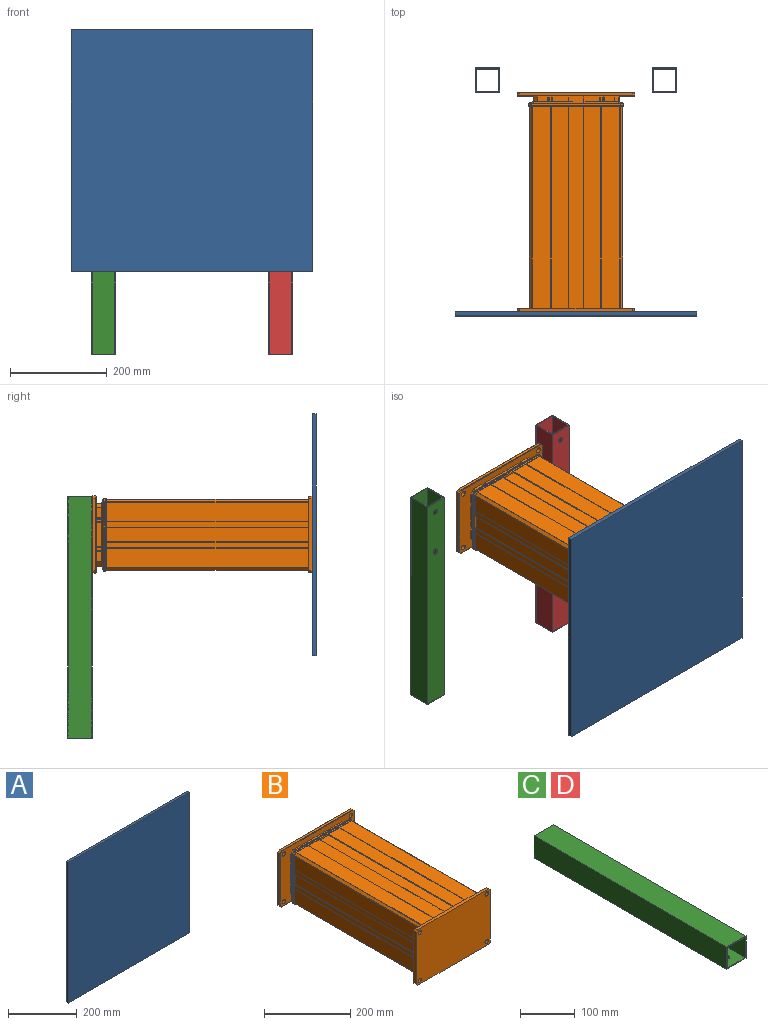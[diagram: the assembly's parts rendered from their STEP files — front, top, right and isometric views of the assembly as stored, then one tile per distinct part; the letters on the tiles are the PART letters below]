
ASSEMBLY  parts=4 mates=3
PART A: 6 faces, bbox 500x8x500 mm
  f0: plane 500x8mm, normal (0,0,1), area 4000mm2, adj f1,f3,f4,f5
  f1: plane 500x8mm, normal (-1,0,0), area 4000mm2, adj f0,f2,f4,f5
  f2: plane 500x8mm, normal (0,0,-1), area 4000mm2, adj f1,f3,f4,f5
  f3: plane 500x8mm, normal (1,0,0), area 4000mm2, adj f0,f2,f4,f5
  f4: plane 500x500mm, normal (0,-1,0), area 250000mm2, adj f0,f1,f2,f3
  f5: plane 500x500mm, normal (0,1,0), area 250000mm2, adj f0,f1,f2,f3
PART B: 367 faces, bbox 245x456x161 mm
  f0: plane 8x4.41mm, normal (0.71,0,0.71), area 49.9mm2, adj f357,f360,f361,f366
  f1: plane 8x4.41mm, normal (0.71,0,-0.71), area 49.9mm2, adj f357,f358,f361,f366
  f2: plane 8x4.41mm, normal (-0.71,0,-0.71), area 49.9mm2, adj f358,f359,f361,f366
  f3: plane 8x4.41mm, normal (-0.71,0,0.71), area 49.9mm2, adj f359,f360,f361,f366
  f4: plane 417x30.8mm, normal (1,0,0), area 12843.6mm2, adj f10,f11,f75,f361
  f5: cylinder r=0.5mm len=417mm, axis (0,1,0), area 491.3mm2, adj f74,f75,f342,f361
  f6: cylinder r=0.5mm len=417mm, axis (0,1,0), area 491.3mm2, adj f22,f23,f75,f361
  f7: cylinder r=0.5mm len=417mm, axis (0,-1,0), area 491.3mm2, adj f23,f24,f75,f361
  f8: cylinder r=0.5mm len=417mm, axis (0,1,0), area 163.8mm2, adj f26,f27,f75,f361
  f9: cylinder r=0.5mm len=417mm, axis (0,1,0), area 163.8mm2, adj f35,f36,f75,f361
  f10: cylinder r=0.5mm len=417mm, axis (0,-1,0), area 491.3mm2, adj f4,f38,f75,f361
  f11: cylinder r=0.5mm len=417mm, axis (0,1,0), area 491.3mm2, adj f4,f39,f75,f361
  f12: cylinder r=0.5mm len=417mm, axis (0,1,0), area 491.3mm2, adj f55,f56,f75,f361
  f13: cylinder r=0.5mm len=417mm, axis (0,-1,0), area 491.3mm2, adj f56,f57,f75,f361
  f14: cylinder r=0.5mm len=417mm, axis (0,-1,0), area 491.3mm2, adj f73,f74,f75,f361
  f15: plane 15.7x0.21mm, normal (0.71,0,-0.71), area 4.6mm2, adj f16,f18,f84,f313
  f16: cylinder r=0.5mm len=15.7mm, axis (0,-1,0), area 6.2mm2, adj f15,f17,f84,f313
  f17: plane 29.59x15.7mm, normal (0,0,-1), area 430.9mm2, adj f16,f81,f84,f167,f312,f313,f319
  f18: cylinder r=0.5mm len=15.7mm, axis (0,1,0), area 6.2mm2, adj f15,f84,f313,f356
  f19: plane 132.51x82.11mm, normal (0,1,0), area 403.8mm2, adj f80,f168,f169,f170,f171,f172,f173,f174
  f20: plane 417x35.73mm, normal (0,0,-1), area 14898.9mm2, adj f21,f75,f355,f361
  f21: cylinder r=0.5mm len=417mm, axis (0,-1,0), area 491.3mm2, adj f20,f22,f75,f361
  f22: plane 417x1.04mm, normal (0.71,0,0.71), area 615mm2, adj f6,f21,f75,f361
  f23: plane 417x30.8mm, normal (0,0,-1), area 12843.6mm2, adj f6,f7,f75,f361
  f24: plane 417x1.04mm, normal (-0.71,0,0.71), area 615mm2, adj f7,f25,f75,f361
  f25: cylinder r=0.5mm len=417mm, axis (0,1,0), area 491.3mm2, adj f24,f26,f75,f361
  f26: plane 417x35.73mm, normal (0,0,-1), area 14898.9mm2, adj f8,f25,f75,f361
  f27: plane 417x0.21mm, normal (-0.71,0,-0.71), area 122.1mm2, adj f8,f28,f75,f361
  f28: cylinder r=0.5mm len=417mm, axis (0,-1,0), area 163.8mm2, adj f27,f29,f75,f361
  f29: plane 417x38.88mm, normal (0,0,-1), area 16212.4mm2, adj f28,f30,f75,f361
  f30: cylinder r=1mm len=417mm, axis (0,-1,0), area 327.5mm2, adj f29,f31,f75,f361
  f31: plane 417x5.41mm, normal (0.71,0,-0.71), area 3192.9mm2, adj f30,f32,f75,f361
  f32: cylinder r=1mm len=417mm, axis (0,-1,0), area 327.5mm2, adj f31,f33,f75,f361
  f33: plane 417x38.88mm, normal (1,0,0), area 16212.4mm2, adj f32,f34,f75,f361
  f34: cylinder r=0.5mm len=417mm, axis (0,-1,0), area 163.8mm2, adj f33,f35,f75,f361
  f35: plane 417x0.21mm, normal (0.71,0,0.71), area 122.1mm2, adj f9,f34,f75,f361
  f36: plane 417x12.23mm, normal (1,0,0), area 5099.4mm2, adj f9,f37,f75,f361
  f37: cylinder r=0.5mm len=417mm, axis (0,-1,0), area 491.3mm2, adj f36,f38,f75,f361
  f38: plane 417x1.04mm, normal (-0.71,0,0.71), area 615mm2, adj f10,f37,f75,f361
  f39: plane 417x1.04mm, normal (-0.71,0,-0.71), area 615mm2, adj f11,f40,f75,f361
  f40: cylinder r=0.5mm len=417mm, axis (0,1,0), area 491.3mm2, adj f39,f41,f75,f361
  f41: plane 417x12.23mm, normal (1,0,0), area 5099.4mm2, adj f40,f42,f75,f361
  f42: cylinder r=0.5mm len=417mm, axis (0,-1,0), area 163.8mm2, adj f41,f43,f75,f361
  f43: plane 417x0.21mm, normal (0.71,0,-0.71), area 122.1mm2, adj f42,f44,f75,f361
  f44: cylinder r=0.5mm len=417mm, axis (0,1,0), area 163.8mm2, adj f43,f45,f75,f361
  f45: plane 417x38.88mm, normal (1,0,0), area 16212.4mm2, adj f44,f46,f75,f361
  f46: cylinder r=1mm len=417mm, axis (0,1,0), area 327.5mm2, adj f45,f47,f75,f361
  f47: plane 417x5.41mm, normal (0.71,0,0.71), area 3192.9mm2, adj f46,f48,f75,f361
  f48: cylinder r=1mm len=417mm, axis (0,1,0), area 327.5mm2, adj f47,f49,f75,f361
  f49: plane 417x38.88mm, normal (0,0,1), area 16212.4mm2, adj f48,f50,f75,f361
  f50: cylinder r=0.5mm len=417mm, axis (0,1,0), area 163.8mm2, adj f49,f51,f75,f361
  f51: plane 417x0.21mm, normal (-0.71,0,0.71), area 122.1mm2, adj f50,f52,f75,f361
  f52: cylinder r=0.5mm len=417mm, axis (0,-1,0), area 163.8mm2, adj f51,f53,f75,f361
  f53: plane 417x35.73mm, normal (0,0,1), area 14898.9mm2, adj f52,f54,f75,f361
  f54: cylinder r=0.5mm len=417mm, axis (0,-1,0), area 491.3mm2, adj f53,f55,f75,f361
  f55: plane 417x1.04mm, normal (-0.71,0,-0.71), area 615mm2, adj f12,f54,f75,f361
  f56: plane 417x30.8mm, normal (0,0,1), area 12843.6mm2, adj f12,f13,f75,f361
  f57: plane 417x1.04mm, normal (0.71,0,-0.71), area 615mm2, adj f13,f58,f75,f361
  f58: cylinder r=0.5mm len=417mm, axis (0,1,0), area 491.3mm2, adj f57,f59,f75,f361
  f59: plane 417x35.73mm, normal (0,0,1), area 14898.9mm2, adj f58,f60,f75,f361
  f60: cylinder r=0.5mm len=417mm, axis (0,1,0), area 163.8mm2, adj f59,f61,f75,f361
  f61: plane 417x0.21mm, normal (0.71,0,0.71), area 122.1mm2, adj f60,f62,f75,f361
  f62: cylinder r=0.5mm len=417mm, axis (0,-1,0), area 163.8mm2, adj f61,f63,f75,f361
  f63: plane 417x38.88mm, normal (0,0,1), area 16212.4mm2, adj f62,f64,f75,f361
  f64: cylinder r=1mm len=417mm, axis (0,-1,0), area 327.5mm2, adj f63,f65,f75,f361
  f65: plane 417x5.41mm, normal (-0.71,0,0.71), area 3192.9mm2, adj f64,f66,f75,f361
  f66: cylinder r=1mm len=417mm, axis (0,-1,0), area 327.5mm2, adj f65,f67,f75,f361
  f67: plane 417x38.88mm, normal (-1,0,0), area 16212.4mm2, adj f66,f68,f75,f361
  f68: cylinder r=0.5mm len=417mm, axis (0,-1,0), area 163.8mm2, adj f67,f69,f75,f361
  f69: plane 417x0.21mm, normal (-0.71,0,-0.71), area 122.1mm2, adj f68,f70,f75,f361
  f70: cylinder r=0.5mm len=417mm, axis (0,1,0), area 163.8mm2, adj f69,f71,f75,f361
  f71: plane 417x12.23mm, normal (-1,0,0), area 5099.4mm2, adj f70,f72,f75,f361
  f72: cylinder r=0.5mm len=417mm, axis (0,-1,0), area 491.3mm2, adj f71,f73,f75,f361
  f73: plane 417x1.04mm, normal (0.71,0,-0.71), area 615mm2, adj f14,f72,f75,f361
  f74: plane 417x30.8mm, normal (-1,0,0), area 12843.6mm2, adj f5,f14,f75,f361
  f75: plane 196.69x149.69mm, normal (0,-1,0), area 1360.8mm2, adj f4,f5,f6,f7,f8,f9,f10,f11
  f76: plane 134.62x2.49mm, normal (-0.97,-0.26,0), area 346.6mm2, adj f75,f77,f252,f288
  f77: cylinder r=1mm len=134.62mm, axis (0,0,-1), area 37.6mm2, adj f76,f78,f253,f287
  f78: plane 135.56x3.55mm, normal (-1,0.02,0), area 344.7mm2, adj f77,f79,f254,f262,f263,f281,f282,f286
  f79: cylinder r=2mm len=99.1mm, axis (0,0,-1), area 239.4mm2, adj f78,f80,f263,f281
  f80: plane 99.58x8.49mm, normal (-0.34,0.94,0), area 843.5mm2, adj f19,f79,f264,f280
  f81: plane 132.63x82.24mm, normal (0,1,0), area 402.4mm2, adj f17,f82,f135,f136,f137,f138,f139,f140
  f82: plane 50.29x11.93mm, normal (1,0,0), area 463.7mm2, adj f81,f83,f84,f124,f125,f130,f131,f132
  f83: cylinder r=1.5mm len=2mm, axis (-1,0,0), area 4.7mm2, adj f82,f84,f119,f133
  f84: plane 242x158mm, normal (0,-1,0), area 15182.1mm2, adj f15,f16,f17,f18,f82,f83,f85,f86
  f85: plane 234x1mm, normal (0,-0.71,0.71), area 330.3mm2, adj f84,f86,f88,f103
  f86: plane 5.41x5.41mm, normal (-0.5,-0.71,0.5), area 9.4mm2, adj f84,f85,f87,f94
  f87: plane 6x5mm, normal (-0.71,0,0.71), area 42.4mm2, adj f86,f88,f91,f93
  f88: plane 234x6mm, normal (0,0,1), area 1404mm2, adj f85,f87,f89,f104
  f89: plane 234x1mm, normal (0,0.71,0.71), area 330.3mm2, adj f88,f90,f91,f105
  f90: plane 242x158mm, normal (0,1,0), area 37816.9mm2, adj f89,f91,f92,f105,f106,f107,f108,f109
  f91: plane 5.41x5.41mm, normal (-0.5,0.71,0.5), area 9.4mm2, adj f87,f89,f90,f92
  f92: plane 150x1mm, normal (-0.71,0.71,0), area 211.5mm2, adj f90,f91,f93,f109
  f93: plane 150x6mm, normal (-1,0,0), area 900mm2, adj f87,f92,f94,f96
  f94: plane 150x1mm, normal (-0.71,-0.71,0), area 211.5mm2, adj f84,f86,f93,f95
  f95: plane 5.41x5.41mm, normal (-0.5,-0.71,-0.5), area 9.4mm2, adj f84,f94,f96,f98
  f96: plane 6x5mm, normal (-0.71,0,-0.71), area 42.4mm2, adj f93,f95,f97,f109
  f97: plane 234x6mm, normal (0,0,-1), area 1404mm2, adj f96,f98,f100,f108
  f98: plane 234x1mm, normal (0,-0.71,-0.71), area 330.3mm2, adj f84,f95,f97,f99
  f99: plane 5.41x5.41mm, normal (0.5,-0.71,-0.5), area 9.4mm2, adj f84,f98,f100,f102
  f100: plane 6x5mm, normal (0.71,0,-0.71), area 42.4mm2, adj f97,f99,f101,f107
  f101: plane 150x6mm, normal (1,0,0), area 900mm2, adj f100,f102,f104,f106
  f102: plane 150x1mm, normal (0.71,-0.71,0), area 211.5mm2, adj f84,f99,f101,f103
  f103: plane 5.41x5.41mm, normal (0.5,-0.71,0.5), area 9.4mm2, adj f84,f85,f102,f104
  f104: plane 6x5mm, normal (0.71,0,0.71), area 42.4mm2, adj f88,f101,f103,f105
  f105: plane 5.41x5.41mm, normal (0.5,0.71,0.5), area 9.4mm2, adj f89,f90,f104,f106
  f106: plane 150x1mm, normal (0.71,0.71,0), area 211.5mm2, adj f90,f101,f105,f107
  f107: plane 5.41x5.41mm, normal (0.5,0.71,-0.5), area 9.4mm2, adj f90,f100,f106,f108
  f108: plane 234x1mm, normal (0,0.71,-0.71), area 330.3mm2, adj f90,f97,f107,f109
  f109: plane 5.41x5.41mm, normal (-0.5,0.71,-0.5), area 9.4mm2, adj f90,f92,f96,f108
  f110: cylinder r=5.5mm len=11mm, axis (0,1,0), area 276.5mm2, adj f84,f90
  f111: cylinder r=5.5mm len=11mm, axis (0,1,0), area 276.5mm2, adj f84,f90
  f112: cylinder r=5.5mm len=11mm, axis (0,1,0), area 276.5mm2, adj f84,f90
  f113: cylinder r=5.5mm len=11mm, axis (0,1,0), area 276.5mm2, adj f84,f90
  f114: plane 7.91x2.65mm, normal (0,0,-1), area 19.3mm2, adj f84,f115,f116,f121,f122,f134
  f115: plane 8.5x6mm, normal (1,0,0), area 30.8mm2, adj f84,f114,f116,f117
  f116: cylinder r=3mm len=6.8mm, axis (1,0,0), area 121.3mm2, adj f114,f115,f117,f134
  f117: plane 7.91x2.65mm, normal (0,0,1), area 19.3mm2, adj f84,f115,f116,f118,f121,f134
  f118: cylinder r=0.5mm len=4mm, axis (0,0,1), area 3.1mm2, adj f84,f117,f119,f121
  f119: torus R=1mm, axis (-1,0,0), area 1.6mm2, adj f83,f118,f120,f121
  f120: cylinder r=0.5mm len=8.5mm, axis (0,1,0), area 6.7mm2, adj f119,f121,f129,f133
  f121: plane 11x10.5mm, normal (1,0,0), area 63.4mm2, adj f114,f117,f118,f119,f120,f122,f123,f126
  f122: cylinder r=0.5mm len=4mm, axis (0,0,1), area 3.1mm2, adj f84,f114,f121,f123
  f123: torus R=1mm, axis (-1,0,0), area 1.6mm2, adj f121,f122,f124,f126
  f124: cylinder r=1.5mm len=2mm, axis (-1,0,0), area 4.7mm2, adj f82,f84,f123,f125
  f125: plane 8.5x2mm, normal (0,0,1), area 17mm2, adj f82,f124,f126,f132
  f126: cylinder r=0.5mm len=8.5mm, axis (0,-1,0), area 6.7mm2, adj f121,f123,f125,f127
  f127: torus R=1mm, axis (-1,0,0), area 1.6mm2, adj f121,f126,f128,f132
  f128: cylinder r=0.5mm len=9mm, axis (0,0,-1), area 7.1mm2, adj f121,f127,f129,f131
  f129: torus R=1mm, axis (-1,0,0), area 1.6mm2, adj f120,f121,f128,f130
  f130: cylinder r=1.5mm len=2mm, axis (-1,0,0), area 4.7mm2, adj f82,f129,f131,f133
  f131: plane 9x2mm, normal (0,-1,0), area 18mm2, adj f82,f128,f130,f132
  f132: cylinder r=1.5mm len=2mm, axis (-1,0,0), area 4.7mm2, adj f82,f125,f127,f131
  f133: plane 8.5x2mm, normal (0,0,-1), area 17mm2, adj f82,f83,f120,f130
  f134: cone r=3.5mm half-angle=45deg, axis (1,0,0), area 29.7mm2, adj f114,f116,f117,f121
  f135: cylinder r=0.5mm len=11.93mm, axis (0,-1,0), area 4.7mm2, adj f81,f82,f84,f136
  f136: plane 11.93x1.51mm, normal (0.71,0,0.71), area 25.4mm2, adj f81,f84,f135,f137
  f137: cylinder r=0.5mm len=11.93mm, axis (0,1,0), area 4.7mm2, adj f81,f84,f136,f138
  f138: plane 11.93x4.79mm, normal (1,0,0), area 57.1mm2, adj f81,f84,f137,f139
  f139: cylinder r=0.5mm len=11.93mm, axis (0,1,0), area 4.7mm2, adj f81,f84,f138,f140
  f140: plane 11.93x2.01mm, normal (0.71,0,-0.71), area 33.9mm2, adj f81,f84,f139,f141
  f141: cylinder r=0.5mm len=11.93mm, axis (0,1,0), area 4.7mm2, adj f81,f84,f140,f142
  f142: plane 20.88x11.93mm, normal (1,0,0), area 249mm2, adj f81,f84,f141,f143
  f143: cylinder r=1mm len=11.93mm, axis (0,1,0), area 9.4mm2, adj f81,f84,f142,f144
  f144: plane 11.93x8.41mm, normal (0.71,0,0.71), area 141.9mm2, adj f81,f84,f143,f145
  f145: cylinder r=1mm len=11.93mm, axis (0,1,0), area 9.4mm2, adj f81,f84,f144,f146
  f146: plane 20.88x11.93mm, normal (0,0,1), area 249mm2, adj f81,f84,f145,f147
  f147: cylinder r=0.5mm len=11.93mm, axis (0,1,0), area 4.7mm2, adj f81,f84,f146,f148
  f148: plane 11.93x2.01mm, normal (-0.71,0,0.71), area 33.9mm2, adj f81,f84,f147,f149
  f149: cylinder r=0.5mm len=11.93mm, axis (0,1,0), area 4.7mm2, adj f81,f84,f148,f150
  f150: plane 11.93x4.79mm, normal (0,0,1), area 57.1mm2, adj f81,f84,f149,f151
  f151: cylinder r=0.5mm len=11.93mm, axis (0,1,0), area 4.7mm2, adj f81,f84,f150,f152
  f152: plane 11.93x1.51mm, normal (0.71,0,0.71), area 25.4mm2, adj f81,f84,f151,f153
  f153: cylinder r=0.5mm len=11.93mm, axis (0,1,0), area 4.7mm2, adj f81,f84,f152,f154
  f154: plane 32.94x15.7mm, normal (0,0,1), area 401mm2, adj f81,f84,f153,f155,f214,f215,f216
  f155: plane 10.11x3.65mm, normal (-0.71,0.71,0), area 30.5mm2, adj f81,f154,f156,f216,f218
  f156: cylinder r=0.5mm len=8.51mm, axis (0.32,0.32,-0.89), area 3.9mm2, adj f81,f155,f157,f218
  f157: plane 56.4x8.49mm, normal (0,0.94,0.34), area 463.7mm2, adj f81,f156,f158,f219
  f158: bspline ~19.11x12.13mm, area 130.3mm2, adj f81,f157,f159,f229
  f159: bspline ~15.81x15.8mm, area 102.6mm2, adj f81,f158,f160,f230,f232,f234
  f160: bspline ~19.13x12.14mm, area 130.3mm2, adj f81,f159,f161,f235
  f161: plane 99.58x8.49mm, normal (0.34,0.94,0), area 843.7mm2, adj f81,f160,f162,f236
  f162: bspline ~19.13x12.14mm, area 130.3mm2, adj f81,f161,f163,f317
  f163: bspline ~15.81x15.8mm, area 102.6mm2, adj f81,f162,f164,f272,f274,f316
  f164: bspline ~18.86x12.14mm, area 130.3mm2, adj f81,f163,f165,f275
  f165: plane 68.26x8.35mm, normal (0,0.94,-0.34), area 566mm2, adj f81,f164,f166,f276
  f166: cylinder r=0.5mm len=8.51mm, axis (0.32,0.32,0.89), area 3.9mm2, adj f81,f165,f167,f311
  f167: plane 10.61x3.65mm, normal (-0.71,0.71,0), area 33.1mm2, adj f17,f81,f166,f311,f312
  f168: cylinder r=0.5mm len=11.93mm, axis (0,1,0), area 4.7mm2, adj f19,f84,f169,f356
  f169: plane 11.93x1.51mm, normal (-0.71,0,-0.71), area 25.4mm2, adj f19,f84,f168,f170
  f170: cylinder r=0.5mm len=11.93mm, axis (0,1,0), area 4.7mm2, adj f19,f84,f169,f171
  f171: plane 11.93x4.79mm, normal (0,0,-1), area 57.1mm2, adj f19,f84,f170,f172
  f172: cylinder r=0.5mm len=11.93mm, axis (0,1,0), area 4.7mm2, adj f19,f84,f171,f173
  f173: plane 11.93x2.01mm, normal (0.71,0,-0.71), area 33.9mm2, adj f19,f84,f172,f174
  f174: cylinder r=0.5mm len=11.93mm, axis (0,1,0), area 4.7mm2, adj f19,f84,f173,f175
  f175: plane 20.88x11.93mm, normal (0,0,-1), area 249mm2, adj f19,f84,f174,f176
  f176: cylinder r=1mm len=11.93mm, axis (0,1,0), area 9.4mm2, adj f19,f84,f175,f177
  f177: plane 11.93x8.41mm, normal (-0.71,0,-0.71), area 141.9mm2, adj f19,f84,f176,f178
  f178: cylinder r=1mm len=11.93mm, axis (0,1,0), area 9.4mm2, adj f19,f84,f177,f179
  f179: plane 20.88x11.93mm, normal (-1,0,0), area 249mm2, adj f19,f84,f178,f180
  f180: cylinder r=0.5mm len=11.93mm, axis (0,1,0), area 4.7mm2, adj f19,f84,f179,f181
  f181: plane 11.93x2.01mm, normal (-0.71,0,0.71), area 33.9mm2, adj f19,f84,f180,f182
  f182: cylinder r=0.5mm len=11.93mm, axis (0,1,0), area 4.7mm2, adj f19,f84,f181,f183
  f183: plane 11.93x4.79mm, normal (-1,0,0), area 57.1mm2, adj f19,f84,f182,f184
  f184: cylinder r=0.5mm len=11.93mm, axis (0,1,0), area 4.7mm2, adj f19,f84,f183,f185
  f185: plane 11.93x1.51mm, normal (-0.71,0,-0.71), area 25.4mm2, adj f19,f84,f184,f186
  f186: cylinder r=0.5mm len=11.93mm, axis (0,-1,0), area 4.7mm2, adj f19,f84,f185,f187
  f187: plane 50.29x11.93mm, normal (-1,0,0), area 599.7mm2, adj f19,f84,f186,f188
  f188: cylinder r=0.5mm len=11.93mm, axis (0,1,0), area 4.7mm2, adj f19,f84,f187,f189
  f189: plane 11.93x1.51mm, normal (-0.71,0,0.71), area 25.4mm2, adj f19,f84,f188,f190
  f190: cylinder r=0.5mm len=11.93mm, axis (0,-1,0), area 4.7mm2, adj f19,f84,f189,f191
  f191: plane 11.93x4.79mm, normal (-1,0,0), area 57.1mm2, adj f19,f84,f190,f192
  f192: cylinder r=0.5mm len=11.93mm, axis (0,-1,0), area 4.7mm2, adj f19,f84,f191,f193
  f193: plane 11.93x2.01mm, normal (-0.71,0,-0.71), area 33.9mm2, adj f19,f84,f192,f194
  f194: cylinder r=0.5mm len=11.93mm, axis (0,-1,0), area 4.7mm2, adj f19,f84,f193,f195
  f195: plane 20.88x11.93mm, normal (-1,0,0), area 249mm2, adj f19,f84,f194,f196
  f196: cylinder r=1mm len=11.93mm, axis (0,-1,0), area 9.4mm2, adj f19,f84,f195,f197
  f197: plane 11.93x8.41mm, normal (-0.71,0,0.71), area 141.9mm2, adj f19,f84,f196,f198
  f198: cylinder r=1mm len=11.93mm, axis (0,-1,0), area 9.4mm2, adj f19,f84,f197,f199
  f199: plane 20.88x11.93mm, normal (0,0,1), area 249mm2, adj f19,f84,f198,f200
  f200: cylinder r=0.5mm len=11.93mm, axis (0,-1,0), area 4.7mm2, adj f19,f84,f199,f201
  f201: plane 11.93x2.01mm, normal (0.71,0,0.71), area 33.9mm2, adj f19,f84,f200,f202
  f202: cylinder r=0.5mm len=11.93mm, axis (0,-1,0), area 4.7mm2, adj f19,f84,f201,f203
  f203: plane 11.93x4.79mm, normal (0,0,1), area 57.1mm2, adj f19,f84,f202,f204
  f204: cylinder r=0.5mm len=11.93mm, axis (0,-1,0), area 4.7mm2, adj f19,f84,f203,f205
  f205: plane 11.93x1.51mm, normal (-0.71,0,0.71), area 25.4mm2, adj f19,f84,f204,f206
  f206: cylinder r=0.5mm len=11.93mm, axis (0,-1,0), area 4.7mm2, adj f19,f84,f205,f207
  f207: plane 32.94x11.93mm, normal (0,0,1), area 392.8mm2, adj f19,f84,f206,f208
  f208: cylinder r=0.5mm len=11.93mm, axis (0,-1,0), area 4.7mm2, adj f19,f84,f207,f209
  f209: plane 11.93x0.21mm, normal (0.71,0,0.71), area 3.5mm2, adj f19,f84,f208,f210
  f210: cylinder r=0.5mm len=11.93mm, axis (0,1,0), area 4.7mm2, adj f19,f84,f209,f211
  f211: plane 29.59x15.7mm, normal (0,0,1), area 430.9mm2, adj f19,f84,f210,f212,f215,f221,f222
  f212: cylinder r=0.5mm len=15.7mm, axis (0,-1,0), area 6.2mm2, adj f84,f211,f213,f215
  f213: plane 15.7x0.21mm, normal (-0.71,0,0.71), area 4.6mm2, adj f84,f212,f214,f215
  f214: cylinder r=0.5mm len=15.7mm, axis (0,1,0), area 6.2mm2, adj f84,f154,f213,f215
  f215: plane 19.59x10.73mm, normal (0,1,0), area 209.8mm2, adj f154,f211,f212,f213,f214,f216,f221,f318
  f216: cylinder r=0.5mm len=10.23mm, axis (0,0,-1), area 4mm2, adj f154,f155,f215,f217
  f217: bspline ~0.86x0.65mm, area 0.4mm2, adj f216,f218,f219,f318
  f218: bspline ~1.36x1.26mm, area 0.7mm2, adj f155,f156,f217,f219
  f219: cylinder r=2mm len=146.1mm, axis (-1,0,0), area 315mm2, adj f157,f217,f218,f220,f223,f225,f227,f228
  f220: bspline ~0.86x0.65mm, area 0.4mm2, adj f219,f221,f223,f318
  f221: cylinder r=0.5mm len=10.73mm, axis (0,0,1), area 4.2mm2, adj f211,f215,f220,f222
  f222: plane 10.61x3.65mm, normal (0.71,0.71,0), area 33.1mm2, adj f19,f211,f221,f223,f224
  f223: bspline ~1.36x1.27mm, area 0.7mm2, adj f219,f220,f222,f224
  f224: cylinder r=0.5mm len=8.51mm, axis (0.32,-0.32,0.89), area 3.9mm2, adj f19,f222,f223,f225
  f225: plane 68.26x8.35mm, normal (0,0.94,0.34), area 566mm2, adj f19,f219,f224,f226
  f226: bspline ~19.11x12.14mm, area 130.3mm2, adj f19,f225,f227,f257
  f227: bspline ~18.52x2.29mm, area 42.5mm2, adj f219,f226,f228,f258
  f228: plane 182.55x3.54mm, normal (0,0.02,1), area 465.7mm2, adj f219,f227,f229,f230,f246,f258,f260,f265
  f229: bspline ~18.52x2.29mm, area 42.5mm2, adj f158,f219,f228,f230
  f230: bspline ~2.21x1.83mm, area 1.5mm2, adj f159,f228,f229,f231
  f231: sphere r=2mm, area 2.4mm2, adj f230,f232,f265
  f232: bspline ~9.12x9.12mm, area 24.7mm2, adj f159,f231,f233,f266
  f233: sphere r=2mm, area 2.3mm2, adj f232,f234,f267
  f234: bspline ~2.21x1.83mm, area 1.5mm2, adj f159,f233,f235,f237
  f235: bspline ~18.67x2.29mm, area 42.5mm2, adj f160,f234,f236,f237
  f236: cylinder r=2mm len=99.1mm, axis (0,0,1), area 239.4mm2, adj f161,f235,f237,f317
  f237: plane 135.56x3.55mm, normal (1,0.02,0), area 344.6mm2, adj f234,f235,f236,f238,f267,f270,f316,f317
  f238: cylinder r=1mm len=134.62mm, axis (0,0,1), area 37.6mm2, adj f237,f239,f241,f269
  f239: plane 134.62x2.49mm, normal (0.97,-0.26,0), area 346.6mm2, adj f75,f238,f240,f268
  f240: cylinder r=2mm len=2.53mm, axis (0.26,0.96,0.11), area 3.9mm2, adj f75,f239,f241,f243
  f241: bspline ~1.71x0.75mm, area 0.4mm2, adj f238,f240,f242,f267
  f242: cylinder r=1mm len=6.25mm, axis (-0.71,0,0.71), area 2.5mm2, adj f241,f243,f245,f266
  f243: plane 6.5x6.5mm, normal (0.68,-0.26,0.68), area 22mm2, adj f75,f240,f242,f244
  f244: cylinder r=2mm len=2.53mm, axis (0.11,0.96,0.26), area 3.9mm2, adj f75,f243,f245,f247
  f245: bspline ~1.72x0.75mm, area 0.4mm2, adj f242,f244,f246,f265
  f246: cylinder r=1mm len=181.62mm, axis (-1,0,0), area 50.8mm2, adj f228,f245,f247,f249
  f247: plane 181.62x2.49mm, normal (0,-0.26,0.97), area 467.8mm2, adj f75,f244,f246,f248
  f248: cylinder r=2mm len=2.53mm, axis (0.11,-0.96,-0.26), area 3.9mm2, adj f75,f247,f249,f251
  f249: bspline ~1.72x0.75mm, area 0.4mm2, adj f246,f248,f250,f260
  f250: cylinder r=1mm len=6.25mm, axis (-0.71,0,-0.71), area 2.5mm2, adj f249,f251,f253,f261
  f251: plane 6.5x6.5mm, normal (-0.68,-0.26,0.68), area 22mm2, adj f75,f248,f250,f252
  f252: cylinder r=2mm len=2.53mm, axis (0.26,-0.96,-0.11), area 3.9mm2, adj f75,f76,f251,f253
  f253: bspline ~1.71x0.75mm, area 0.4mm2, adj f77,f250,f252,f254
  f254: cylinder r=2mm len=2.45mm, axis (-0.02,-1,0.01), area 3.8mm2, adj f78,f253,f255,f261
  f255: sphere r=2mm, area 2.3mm2, adj f254,f256,f262
  f256: bspline ~9.12x9.12mm, area 24.7mm2, adj f255,f257,f259,f261
  f257: bspline ~15.8x15.69mm, area 102.6mm2, adj f19,f226,f256,f258,f262,f264
  f258: bspline ~2.21x1.83mm, area 1.5mm2, adj f227,f228,f257,f259
  f259: sphere r=2mm, area 2.3mm2, adj f256,f258,f260
  f260: cylinder r=2mm len=2.45mm, axis (-0.01,-1,0.02), area 3.8mm2, adj f228,f249,f259,f261
  f261: plane 6.29x6.29mm, normal (-0.71,0.02,0.71), area 23.6mm2, adj f250,f254,f256,f260
  f262: bspline ~2.21x1.83mm, area 1.5mm2, adj f78,f255,f257,f263
  f263: bspline ~18.67x2.29mm, area 42.5mm2, adj f78,f79,f262,f264
  f264: bspline ~19.13x12.14mm, area 130.3mm2, adj f19,f80,f257,f263
  f265: cylinder r=2mm len=2.45mm, axis (-0.01,1,-0.02), area 3.8mm2, adj f228,f231,f245,f266
  f266: plane 6.29x6.29mm, normal (0.71,0.02,0.71), area 23.6mm2, adj f232,f242,f265,f267
  f267: cylinder r=2mm len=2.45mm, axis (-0.02,1,-0.01), area 3.8mm2, adj f233,f237,f241,f266
  f268: cylinder r=2mm len=2.53mm, axis (-0.26,-0.96,0.11), area 3.9mm2, adj f75,f239,f269,f303
  f269: bspline ~1.71x0.75mm, area 0.4mm2, adj f238,f268,f270,f304
  f270: cylinder r=2mm len=2.45mm, axis (0.02,-1,-0.01), area 3.8mm2, adj f237,f269,f271,f305
  f271: sphere r=2mm, area 2.4mm2, adj f270,f272,f316
  f272: bspline ~9.12x9.12mm, area 24.7mm2, adj f163,f271,f273,f305
  f273: sphere r=2mm, area 2.4mm2, adj f272,f274,f300
  f274: bspline ~2.21x1.83mm, area 1.5mm2, adj f163,f273,f275,f295
  f275: bspline ~18.52x2.29mm, area 42.5mm2, adj f164,f274,f276,f295
  f276: cylinder r=2mm len=146.1mm, axis (1,0,0), area 315mm2, adj f165,f275,f277,f295,f296,f307,f308,f309
  f277: plane 56.4x8.49mm, normal (0,0.94,-0.34), area 463.7mm2, adj f19,f276,f278,f306
  f278: bspline ~19.11x12.13mm, area 130.3mm2, adj f19,f277,f279,f296
  f279: bspline ~15.81x15.69mm, area 102.6mm2, adj f19,f278,f280,f282,f284,f297
  f280: bspline ~19.13x12.14mm, area 130.3mm2, adj f19,f80,f279,f281
  f281: bspline ~18.67x2.29mm, area 42.5mm2, adj f78,f79,f280,f282
  f282: bspline ~2.21x1.83mm, area 1.5mm2, adj f78,f279,f281,f283
  f283: sphere r=2mm, area 2.3mm2, adj f282,f284,f286
  f284: bspline ~9.12x9.12mm, area 24.7mm2, adj f279,f283,f285,f298
  f285: plane 6.29x6.29mm, normal (-0.71,0.02,-0.71), area 23.6mm2, adj f284,f286,f290,f299
  f286: cylinder r=2mm len=2.45mm, axis (0.02,1,0.01), area 3.8mm2, adj f78,f283,f285,f287
  f287: bspline ~1.71x0.75mm, area 0.4mm2, adj f77,f286,f288,f290
  f288: cylinder r=2mm len=2.53mm, axis (-0.26,0.96,-0.11), area 3.9mm2, adj f75,f76,f287,f289
  f289: plane 6.5x6.5mm, normal (-0.68,-0.26,-0.68), area 22mm2, adj f75,f288,f290,f292
  f290: cylinder r=1mm len=6.25mm, axis (0.71,0,-0.71), area 2.5mm2, adj f285,f287,f289,f291
  f291: bspline ~1.72x0.75mm, area 0.4mm2, adj f290,f292,f294,f299
  f292: cylinder r=2mm len=2.53mm, axis (-0.11,0.96,-0.26), area 3.9mm2, adj f75,f289,f291,f293
  f293: plane 181.62x2.49mm, normal (0,-0.26,-0.97), area 467.8mm2, adj f75,f292,f294,f302
  f294: cylinder r=1mm len=181.62mm, axis (1,0,0), area 50.8mm2, adj f291,f293,f295,f301
  f295: plane 182.55x3.54mm, normal (0,0.02,-1), area 465.7mm2, adj f274,f275,f276,f294,f296,f297,f299,f300
  f296: bspline ~18.52x2.29mm, area 42.5mm2, adj f276,f278,f295,f297
  f297: bspline ~2.21x1.83mm, area 1.5mm2, adj f279,f295,f296,f298
  f298: sphere r=2mm, area 2.4mm2, adj f284,f297,f299
  f299: cylinder r=2mm len=2.45mm, axis (0.01,1,0.02), area 3.8mm2, adj f285,f291,f295,f298
  f300: cylinder r=2mm len=2.45mm, axis (0.01,-1,-0.02), area 3.8mm2, adj f273,f295,f301,f305
  f301: bspline ~1.72x0.75mm, area 0.4mm2, adj f294,f300,f302,f304
  f302: cylinder r=2mm len=2.53mm, axis (-0.11,-0.96,0.26), area 3.9mm2, adj f75,f293,f301,f303
  f303: plane 6.5x6.5mm, normal (0.68,-0.26,-0.68), area 22mm2, adj f75,f268,f302,f304
  f304: cylinder r=1mm len=6.25mm, axis (0.71,0,0.71), area 2.5mm2, adj f269,f301,f303,f305
  f305: plane 6.29x6.29mm, normal (0.71,0.02,-0.71), area 23.6mm2, adj f270,f272,f300,f304
  f306: cylinder r=0.5mm len=8.51mm, axis (0.32,-0.32,-0.89), area 3.9mm2, adj f19,f277,f307,f315
  f307: bspline ~1.35x1.28mm, area 0.7mm2, adj f276,f306,f308,f315
  f308: bspline ~0.87x0.66mm, area 0.4mm2, adj f276,f307,f309,f314
  f309: cylinder r=0.5mm len=19.59mm, axis (1,0,0), area 12.1mm2, adj f276,f308,f310,f313
  f310: bspline ~0.87x0.66mm, area 0.4mm2, adj f276,f309,f311,f312
  f311: bspline ~1.34x1.27mm, area 0.7mm2, adj f166,f167,f276,f310
  f312: cylinder r=0.5mm len=10.72mm, axis (0,0,-1), area 4.2mm2, adj f17,f167,f310,f313
  f313: plane 19.59x10.72mm, normal (0,1,0), area 209.7mm2, adj f15,f16,f17,f18,f309,f312,f314,f356
  f314: cylinder r=0.5mm len=10.22mm, axis (0,0,1), area 4mm2, adj f308,f313,f315,f356
  f315: plane 10.11x3.65mm, normal (0.71,0.71,0), area 30.5mm2, adj f19,f306,f307,f314,f356
  f316: bspline ~2.21x1.83mm, area 1.5mm2, adj f163,f237,f271,f317
  f317: bspline ~18.67x2.29mm, area 42.5mm2, adj f162,f236,f237,f316
  f318: cylinder r=0.5mm len=19.59mm, axis (1,0,0), area 12.1mm2, adj f215,f217,f219,f220
  f319: cylinder r=0.5mm len=11.93mm, axis (0,1,0), area 4.7mm2, adj f17,f81,f84,f320
  f320: plane 11.93x0.21mm, normal (-0.71,0,-0.71), area 3.5mm2, adj f81,f84,f319,f321
  f321: cylinder r=0.5mm len=11.93mm, axis (0,-1,0), area 4.7mm2, adj f81,f84,f320,f322
  f322: plane 32.94x11.93mm, normal (0,0,-1), area 392.8mm2, adj f81,f84,f321,f323
  f323: cylinder r=0.5mm len=11.93mm, axis (0,-1,0), area 4.7mm2, adj f81,f84,f322,f324
  f324: plane 11.93x1.51mm, normal (0.71,0,-0.71), area 25.4mm2, adj f81,f84,f323,f325
  f325: cylinder r=0.5mm len=11.93mm, axis (0,-1,0), area 4.7mm2, adj f81,f84,f324,f326
  f326: plane 11.93x4.79mm, normal (0,0,-1), area 57.1mm2, adj f81,f84,f325,f327
  f327: cylinder r=0.5mm len=11.93mm, axis (0,-1,0), area 4.7mm2, adj f81,f84,f326,f328
  f328: plane 11.93x2.01mm, normal (-0.71,0,-0.71), area 33.9mm2, adj f81,f84,f327,f329
  f329: cylinder r=0.5mm len=11.93mm, axis (0,-1,0), area 4.7mm2, adj f81,f84,f328,f330
  f330: plane 20.88x11.93mm, normal (0,0,-1), area 249mm2, adj f81,f84,f329,f331
  f331: cylinder r=1mm len=11.93mm, axis (0,-1,0), area 9.4mm2, adj f81,f84,f330,f332
  f332: plane 11.93x8.41mm, normal (0.71,0,-0.71), area 141.9mm2, adj f81,f84,f331,f333
  f333: cylinder r=1mm len=11.93mm, axis (0,-1,0), area 9.4mm2, adj f81,f84,f332,f334
  f334: plane 20.88x11.93mm, normal (1,0,0), area 249mm2, adj f81,f84,f333,f335
  f335: cylinder r=0.5mm len=11.93mm, axis (0,-1,0), area 4.7mm2, adj f81,f84,f334,f336
  f336: plane 11.93x2.01mm, normal (0.71,0,0.71), area 33.9mm2, adj f81,f84,f335,f337
  f337: cylinder r=0.5mm len=11.93mm, axis (0,-1,0), area 4.7mm2, adj f81,f84,f336,f338
  f338: plane 11.93x4.79mm, normal (1,0,0), area 57.1mm2, adj f81,f84,f337,f339
  f339: cylinder r=0.5mm len=11.93mm, axis (0,-1,0), area 4.7mm2, adj f81,f84,f338,f340
  f340: plane 11.93x1.51mm, normal (0.71,0,-0.71), area 25.4mm2, adj f81,f84,f339,f341
  f341: cylinder r=0.5mm len=11.93mm, axis (0,1,0), area 4.7mm2, adj f81,f82,f84,f340
  f342: plane 417x1.04mm, normal (0.71,0,0.71), area 615mm2, adj f5,f75,f343,f361
  f343: cylinder r=0.5mm len=417mm, axis (0,1,0), area 491.3mm2, adj f75,f342,f344,f361
  f344: plane 417x12.23mm, normal (-1,0,0), area 5099.4mm2, adj f75,f343,f345,f361
  f345: cylinder r=0.5mm len=417mm, axis (0,-1,0), area 163.8mm2, adj f75,f344,f346,f361
  f346: plane 417x0.21mm, normal (-0.71,0,0.71), area 122.1mm2, adj f75,f345,f347,f361
  f347: cylinder r=0.5mm len=417mm, axis (0,1,0), area 163.8mm2, adj f75,f346,f348,f361
  f348: plane 417x38.88mm, normal (-1,0,0), area 16212.4mm2, adj f75,f347,f349,f361
  f349: cylinder r=1mm len=417mm, axis (0,1,0), area 327.5mm2, adj f75,f348,f350,f361
  f350: plane 417x5.41mm, normal (-0.71,0,-0.71), area 3192.9mm2, adj f75,f349,f351,f361
  f351: cylinder r=1mm len=417mm, axis (0,1,0), area 327.5mm2, adj f75,f350,f352,f361
  f352: plane 417x38.88mm, normal (0,0,-1), area 16212.4mm2, adj f75,f351,f353,f361
  f353: cylinder r=0.5mm len=417mm, axis (0,1,0), area 163.8mm2, adj f75,f352,f354,f361
  f354: plane 417x0.21mm, normal (0.71,0,-0.71), area 122.1mm2, adj f75,f353,f355,f361
  f355: cylinder r=0.5mm len=417mm, axis (0,-1,0), area 163.8mm2, adj f20,f75,f354,f361
  f356: plane 32.94x15.7mm, normal (0,0,-1), area 401mm2, adj f18,f19,f84,f168,f313,f314,f315
  f357: plane 149.17x8mm, normal (1,0,0), area 1193.4mm2, adj f0,f1,f361,f366
  f358: plane 233.17x8mm, normal (0,0,-1), area 1865.4mm2, adj f1,f2,f361,f366
  f359: plane 149.17x8mm, normal (-1,0,0), area 1193.4mm2, adj f2,f3,f361,f366
  f360: plane 233.17x8mm, normal (0,0,1), area 1865.4mm2, adj f0,f3,f361,f366
  f361: plane 242x158mm, normal (0,1,0), area 9864.2mm2, adj f0,f1,f2,f3,f4,f5,f6,f7
  f362: cylinder r=5.5mm len=11mm, axis (0,1,0), area 276.5mm2, adj f361,f366
  f363: cylinder r=5.5mm len=11mm, axis (0,1,0), area 276.5mm2, adj f361,f366
  f364: cylinder r=5.5mm len=11mm, axis (0,1,0), area 276.5mm2, adj f361,f366
  f365: cylinder r=5.5mm len=11mm, axis (0,1,0), area 276.5mm2, adj f361,f366
  f366: plane 242x158mm, normal (0,-1,0), area 37816.9mm2, adj f0,f1,f2,f3,f357,f358,f359,f360
PART C: 12 faces, bbox 50x500x50 mm
  f0: plane 500x50mm, normal (0,0,1), area 25000mm2, adj f1,f7,f8,f9
  f1: plane 500x50mm, normal (-1,0,0), area 25000mm2, adj f0,f2,f8,f9
  f2: plane 500x50mm, normal (0,0,-1), area 24809.9mm2, adj f1,f7,f8,f9,f10,f11
  f3: plane 500x46mm, normal (1,0,0), area 23000mm2, adj f4,f6,f8,f9
  f4: plane 500x46mm, normal (0,0,-1), area 23000mm2, adj f3,f5,f8,f9
  f5: plane 500x46mm, normal (-1,0,0), area 23000mm2, adj f4,f6,f8,f9
  f6: plane 500x46mm, normal (0,0,1), area 22809.9mm2, adj f3,f5,f8,f9,f10,f11
  f7: plane 500x50mm, normal (1,0,0), area 25000mm2, adj f0,f2,f8,f9
  f8: plane 50x50mm, normal (0,-1,0), area 384mm2, adj f0,f1,f2,f3,f4,f5,f6,f7
  f9: plane 50x50mm, normal (0,1,0), area 384mm2, adj f0,f1,f2,f3,f4,f5,f6,f7
  f10: cylinder r=5.5mm len=11mm, axis (0,0,-1), area 69.1mm2, adj f2,f6
  f11: cylinder r=5.5mm len=11mm, axis (0,0,-1), area 69.1mm2, adj f2,f6
PART D: same geometry as C
PLACE A t=(-84.5,-187.62,139)mm
PLACE B t=(-84.5,-378.62,139)mm fixed
PLACE C rot(axis=(-1,0,0),90deg) t=(-267.5,296.38,-32)mm
PLACE D rot(axis=(-1,0,0),90deg) t=(98.5,296.38,-32)mm
MATE fastened D.f2 <-> B.f90  axis (0,-1,0) through (98.5,271.38,218)mm
MATE fastened A.f5 <-> B.f366  axis (0,1,0) through (-84.5,-183.62,139)mm
MATE fastened C.f2 <-> B.f90  axis (0,-1,0) through (-267.5,271.38,218)mm
